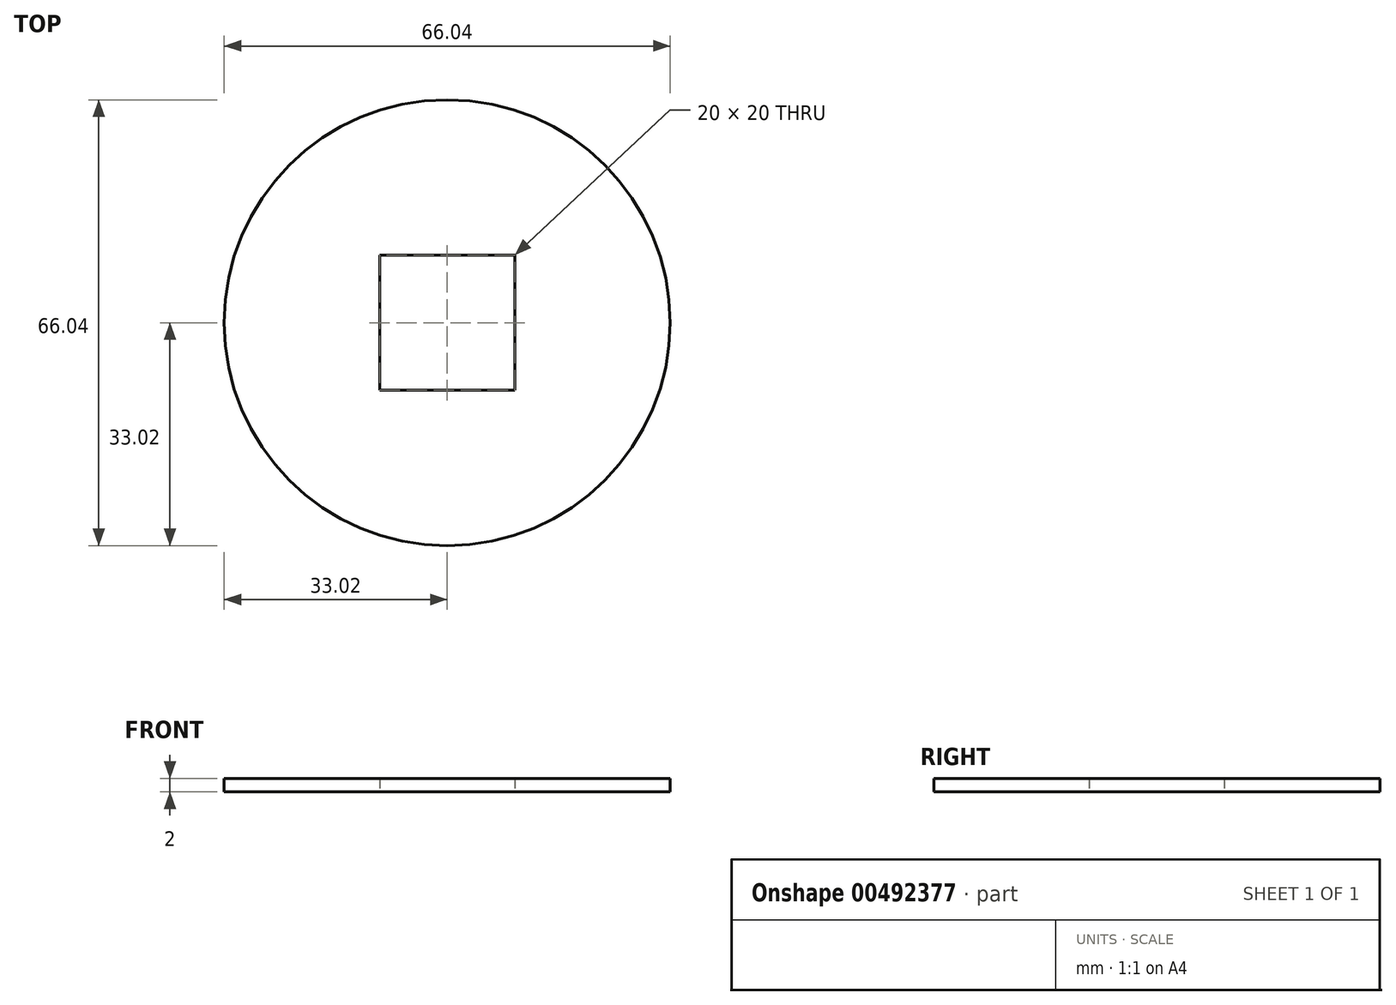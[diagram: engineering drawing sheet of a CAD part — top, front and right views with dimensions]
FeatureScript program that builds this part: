
annotation { "Feature Type Name" : "Feature", "Feature Type Description" : "" }
export const myFeature = defineFeature(function(context is Context, id is Id, definition is map)
    precondition{}
    {
        {
            var Q0;
            Q0=qCreatedBy(makeId("Top.planeOp"),FACE);
            var sketch = newSketch(context, id + "F0", { "sketchPlane" : qUnion([Q0])});
            skCircle(sketch, "E0", {"center": v(0, 0) * mm, "radius": 33.02 * mm});
            skLineSegment(sketch, "E1.bottom", {"start": v(-10, -10) * mm, "end": v(10, -10) * mm});
            skLineSegment(sketch, "E1.top", {"start": v(-10, 10) * mm, "end": v(10, 10) * mm});
            skLineSegment(sketch, "E1.left", {"start": v(-10, -10) * mm, "end": v(-10, 10) * mm});
            skLineSegment(sketch, "E1.right", {"start": v(10, -10) * mm, "end": v(10, 10) * mm});
            skSolve(sketch);
        }
        {
            var Q0;
            Q0=makeQuery(id+"F0.imprint","IMPRINT",FACE,{"disambiguationData":[TD([[makeQuery(id+"F0.imprint","IMPRINT",EDGE,{"derivedFrom":sQuery(id+"F0.wireOp",EDGE,"E0")}),1.0]])]});
            extrude(context, id + "F1", {"entities" : qUnion([Q0]), "depth" : 2 * mm});
        }
    });
